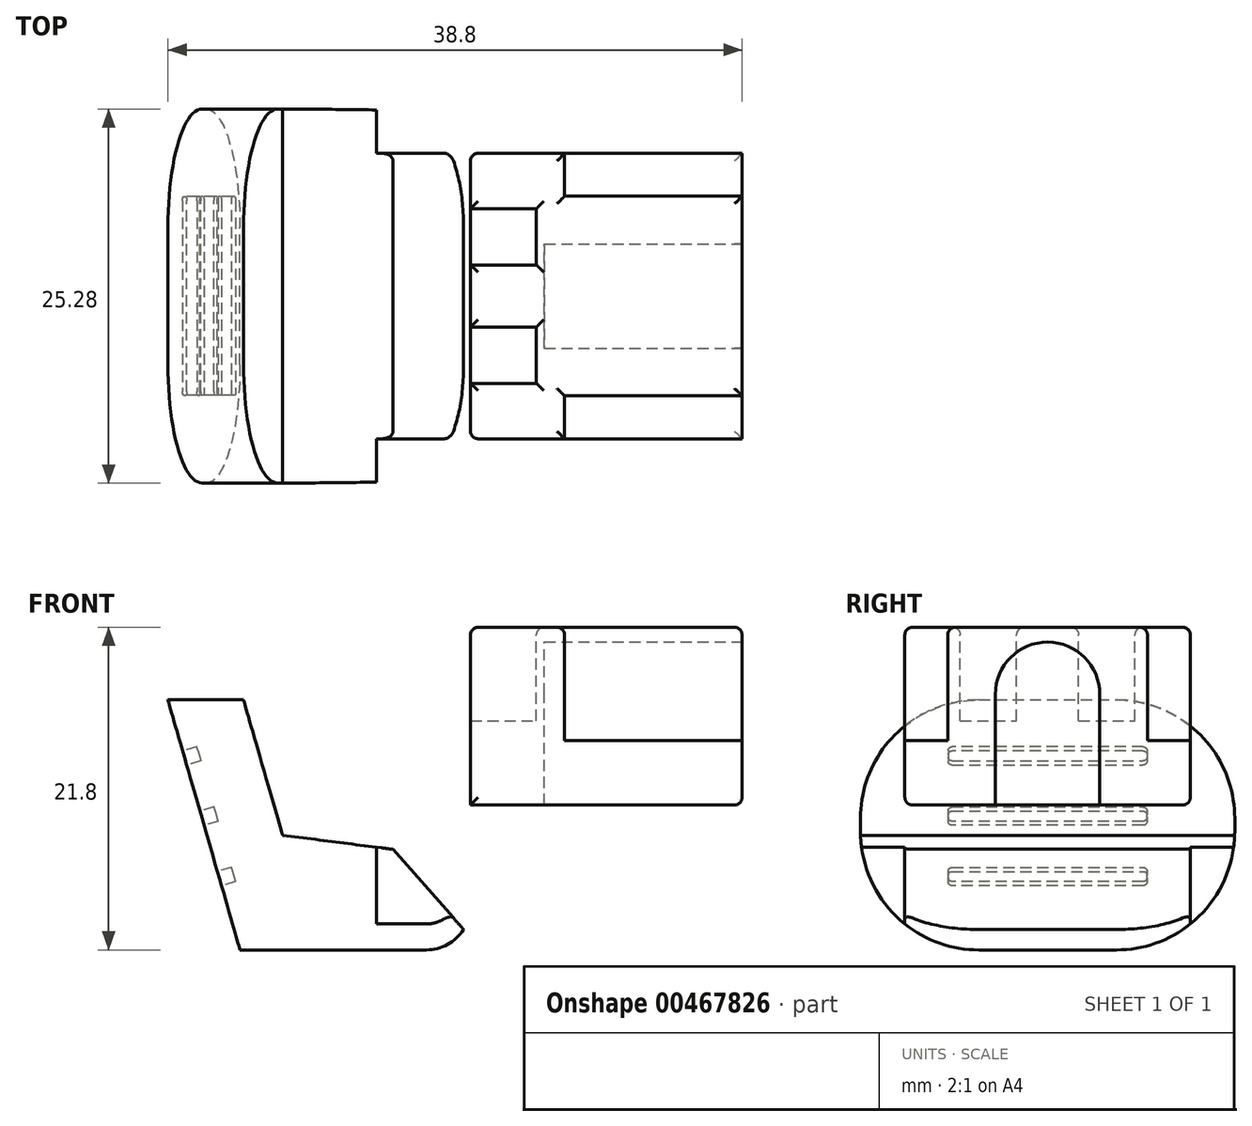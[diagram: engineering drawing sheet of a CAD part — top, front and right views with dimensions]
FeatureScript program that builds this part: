
annotation { "Feature Type Name" : "Feature", "Feature Type Description" : "" }
export const myFeature = defineFeature(function(context is Context, id is Id, definition is map)
    precondition{}
    {
        {
            var Q0;
            Q0=qCreatedBy(makeId("Front.planeOp"),FACE);
            var sketch = newSketch(context, id + "F0", { "sketchPlane" : qUnion([Q0])});
            skLineSegment(sketch, "E0.bottom", {"start": v(-5.4, 12) * mm, "end": v(12.95, 12) * mm});
            skLineSegment(sketch, "E0.top", {"start": v(-5.4, 0) * mm, "end": v(12.95, 0) * mm});
            skLineSegment(sketch, "E0.left", {"start": v(-5.4, 12) * mm, "end": v(-5.4, 0) * mm});
            skLineSegment(sketch, "E0.right", {"start": v(12.95, 12) * mm, "end": v(12.95, 0) * mm});
            skLineSegment(sketch, "E1.bottom", {"start": v(-5.4, 0) * mm, "end": v(-1.18, 0) * mm});
            skLineSegment(sketch, "E1.top", {"start": v(-5.4, -9.8) * mm, "end": v(-1.18, -9.8) * mm});
            skLineSegment(sketch, "E1.left", {"start": v(-5.4, 0) * mm, "end": v(-5.4, -9.8) * mm});
            skLineSegment(sketch, "E1.right", {"start": v(-1.18, 0) * mm, "end": v(-1.18, -9.8) * mm});
            skLineSegment(sketch, "E2", {"start": v(-5.4, -3.67) * mm, "end": v(-18.1, -2.05) * mm});
            skLineSegment(sketch, "E3", {"start": v(-5.4, -9.8) * mm, "end": v(-20.98, -9.8) * mm});
            skLineSegment(sketch, "E4", {"start": v(-20.98, -9.8) * mm, "end": v(-25.85, 7.1) * mm});
            skLineSegment(sketch, "E5", {"start": v(-25.85, 7.1) * mm, "end": v(-20.74, 7.1) * mm});
            skLineSegment(sketch, "E6", {"start": v(-20.74, 7.1) * mm, "end": v(-18.1, -2.05) * mm});
            skSolve(sketch);
        }
        {
            var Q0;
            Q0=makeQuery(id+"F0.imprint","IMPRINT",FACE,{"disambiguationData":[TD([[makeQuery(id+"F0.imprint","IMPRINT",EDGE,{"derivedFrom":sQuery(id+"F0.wireOp",EDGE,"E0.bottom")}),-1.0]])]});
            var Q1;
            {var subQ3=sQuery(id+"F0.wireOp",EDGE,"E1.bottom");Q1=makeQuery(id+"F0.imprint","IMPRINT",FACE,{"disambiguationData":[TD([[makeQuery(id+"F0.imprint","IMPRINT",EDGE,{"derivedFrom":subQ3}),-1.0]])]});}
            var Q2;
            {var subQ1=sQuery(id+"F0.wireOp",EDGE,"E2");Q2=makeQuery(id+"F0.imprint","IMPRINT",FACE,{"disambiguationData":[TD([[makeQuery(id+"F0.imprint","IMPRINT",EDGE,{"derivedFrom":subQ1}),1.0]])]});}
            extrude(context, id + "F1", {"entities" : qUnion([Q0, Q1, Q2]), "endBound" : BoundingType.SYMMETRIC, "depth" : 25.29 * mm});
        }
        {
            var Q0;
            Q0=makeQuery(id+"F1.opExtrude","SWEPT_FACE",FACE,{"disambiguationData":[OSD([sQuery(id+"F0.wireOp",EDGE,"E0.bottom")])]});
            var sketch = newSketch(context, id + "F2", { "sketchPlane" : qUnion([Q0])});
            skLineSegment(sketch, "E7.bottom", {"start": v(12.95, 12.64) * mm, "end": v(-11.75, 12.64) * mm});
            skLineSegment(sketch, "E7.top", {"start": v(12.95, 9.65) * mm, "end": v(-11.75, 9.65) * mm});
            skLineSegment(sketch, "E7.left", {"start": v(12.95, 12.64) * mm, "end": v(12.95, 9.64) * mm});
            skLineSegment(sketch, "E7.right", {"start": v(-11.75, 12.64) * mm, "end": v(-11.75, 9.64) * mm});
            skLineSegment(sketch, "E8.bottom", {"start": v(12.95, -12.64) * mm, "end": v(-11.75, -12.65) * mm});
            skLineSegment(sketch, "E8.top", {"start": v(12.95, -9.65) * mm, "end": v(-11.75, -9.65) * mm});
            skLineSegment(sketch, "E8.left", {"start": v(12.95, -12.64) * mm, "end": v(12.95, -9.65) * mm});
            skLineSegment(sketch, "E8.right", {"start": v(-11.75, -12.65) * mm, "end": v(-11.75, -9.65) * mm});
            skSolve(sketch);
        }
        {
            var Q0;
            Q0 = qSketchRegion(id + "F2", true);
            extrude(context, id + "F3", {"entities" : qUnion([Q0]), "operationType" : NewBodyOperationType.REMOVE, "oppositeDirection" : true, "depth" : 25 * mm});
        }
        {
            var Q0;
            Q0=makeQuery(id+"F1.opExtrude","SWEPT_FACE",FACE,{"disambiguationData":[OSD([sQuery(id+"F0.wireOp",EDGE,"E0.bottom")])]});
            var sketch = newSketch(context, id + "F4", { "sketchPlane" : qUnion([Q0])});
            skLineSegment(sketch, "E9.bottom", {"start": v(-5.4, 5.9) * mm, "end": v(-0.95, 5.9) * mm});
            skLineSegment(sketch, "E9.top", {"start": v(-5.4, 2.1) * mm, "end": v(-0.95, 2.1) * mm});
            skLineSegment(sketch, "E9.left", {"start": v(-5.4, 5.9) * mm, "end": v(-5.4, 2.1) * mm});
            skLineSegment(sketch, "E9.right", {"start": v(-0.95, 5.9) * mm, "end": v(-0.95, 2.1) * mm});
            skLineSegment(sketch, "E10.MirrorCS", {"start": v(-0.95, -5.9) * mm, "end": v(-0.95, -2.1) * mm});
            skLineSegment(sketch, "E11.MirrorCS", {"start": v(-5.4, -5.9) * mm, "end": v(-5.4, -2.1) * mm});
            skLineSegment(sketch, "E12.MirrorCS", {"start": v(-5.4, -5.9) * mm, "end": v(-0.95, -5.9) * mm});
            skLineSegment(sketch, "E13.MirrorCS", {"start": v(-5.4, -2.1) * mm, "end": v(-0.95, -2.1) * mm});
            skLineSegment(sketch, "E14.bottom", {"start": v(12.95, 9.65) * mm, "end": v(0.95, 9.65) * mm});
            skLineSegment(sketch, "E14.top", {"start": v(12.95, 6.75) * mm, "end": v(0.95, 6.74) * mm});
            skLineSegment(sketch, "E14.left", {"start": v(12.95, 9.65) * mm, "end": v(12.95, 6.75) * mm});
            skLineSegment(sketch, "E14.right", {"start": v(0.95, 9.65) * mm, "end": v(0.95, 6.75) * mm});
            skLineSegment(sketch, "E15.MirrorCS", {"start": v(12.95, -6.75) * mm, "end": v(0.95, -6.74) * mm});
            skLineSegment(sketch, "E16.MirrorCS", {"start": v(12.95, -9.65) * mm, "end": v(0.95, -9.65) * mm});
            skLineSegment(sketch, "E17.MirrorCS", {"start": v(12.95, -9.65) * mm, "end": v(12.95, -6.75) * mm});
            skLineSegment(sketch, "E18.MirrorCS", {"start": v(0.95, -9.65) * mm, "end": v(0.95, -6.75) * mm});
            skSolve(sketch);
        }
        {
            var Q0;
            Q0=makeQuery(id+"F4.imprint","IMPRINT",FACE,{"disambiguationData":[TD([[makeQuery(id+"F4.imprint","IMPRINT",EDGE,{"derivedFrom":sQuery(id+"F4.wireOp",EDGE,"E9.bottom")}),-1.0]])]});
            var Q1;
            Q1=makeQuery(id+"F4.imprint","IMPRINT",FACE,{"disambiguationData":[TD([[makeQuery(id+"F4.imprint","IMPRINT",EDGE,{"derivedFrom":sQuery(id+"F4.wireOp",EDGE,"E10.MirrorCS")}),1.0]])]});
            extrude(context, id + "F5", {"entities" : qUnion([Q0, Q1]), "operationType" : NewBodyOperationType.REMOVE, "oppositeDirection" : true, "depth" : 6.3 * mm});
        }
        {
            var Q0;
            Q0=makeQuery(id+"F4.imprint","IMPRINT",FACE,{"disambiguationData":[TD([[makeQuery(id+"F4.imprint","IMPRINT",EDGE,{"derivedFrom":sQuery(id+"F4.wireOp",EDGE,"E14.bottom")}),1.0]])]});
            var Q1;
            Q1=makeQuery(id+"F4.imprint","IMPRINT",FACE,{"disambiguationData":[TD([[makeQuery(id+"F4.imprint","IMPRINT",EDGE,{"derivedFrom":sQuery(id+"F4.wireOp",EDGE,"E15.MirrorCS")}),1.0]])]});
            extrude(context, id + "F6", {"entities" : qUnion([Q0, Q1]), "operationType" : NewBodyOperationType.REMOVE, "oppositeDirection" : true, "depth" : 7.65 * mm});
        }
        {
            var Q0;
            Q0=makeQuery(id+"F1.opExtrude","SWEPT_FACE",FACE,{"disambiguationData":[OSD([sQuery(id+"F0.wireOp",EDGE,"E0.right")])]});
            var sketch = newSketch(context, id + "F7", { "sketchPlane" : qUnion([Q0])});
            skLineSegment(sketch, "E19", {"start": v(-3.53, 0) * mm, "end": v(-3.53, 7.47) * mm});
            skPoint(sketch, "E20.startSnap0", {"position": v(-6.75, 8.18) * mm});
            skArc(sketch, "E21", {"start": v(-3.53, 7.47) * mm, "mid": v(-2.5, 9.97) * mm, "end": v(0, 11) * mm});
            skArc(sketch, "E22.MirrorCS", {"start": v(3.53, 7.47) * mm, "mid": v(2.5, 9.97) * mm, "end": v(0, 11) * mm});
            skLineSegment(sketch, "E23.MirrorCS", {"start": v(3.53, 0) * mm, "end": v(3.53, 7.47) * mm});
            skSolve(sketch);
        }
        {
            var Q0;
            {var subQ1=sQuery(id+"F7.wireOp",EDGE,"E19");Q0=makeQuery(id+"F7.imprint","IMPRINT",FACE,{"disambiguationData":[TD([[makeQuery(id+"F7.imprint","IMPRINT",EDGE,{"derivedFrom":subQ1}),-1.0]])]});}
            extrude(context, id + "F8", {"entities" : qUnion([Q0]), "operationType" : NewBodyOperationType.REMOVE, "oppositeDirection" : true, "depth" : 13.36 * mm});
        }
        {
            var Q0;
            Q0=makeQuery(id+"F1.opExtrude","CAP_EDGE",EDGE,{"disambiguationData":[OSD([sQuery(id+"F0.wireOp",EDGE,"E5")])],"isStart":false});
            var Q1;
            Q1=makeQuery(id+"F1.opExtrude","CAP_EDGE",EDGE,{"disambiguationData":[OSD([sQuery(id+"F0.wireOp",EDGE,"E1.top"),sQuery(id+"F0.wireOp",EDGE,"E3")])],"isStart":false});
            var Q2;
            Q2=makeQuery(id+"F1.opExtrude","CAP_EDGE",EDGE,{"disambiguationData":[OSD([sQuery(id+"F0.wireOp",EDGE,"E5")])],"isStart":true});
            var Q3;
            Q3=makeQuery(id+"F1.opExtrude","CAP_EDGE",EDGE,{"disambiguationData":[OSD([sQuery(id+"F0.wireOp",EDGE,"E1.top"),sQuery(id+"F0.wireOp",EDGE,"E3")])],"isStart":true});
            fillet(context, id + "F9", {"entities" : qUnion([Q0, Q1, Q2, Q3]), "radius" : 8 * mm, "tangentPropagation" : true, "allowEdgeOverflow" : false});
        }
        {
            var Q0;
            Q0=makeQuery(id+"F1.opExtrude","SWEPT_FACE",FACE,{"disambiguationData":[OSD([sQuery(id+"F0.wireOp",EDGE,"E4")])]});
            var sketch = newSketch(context, id + "F10", { "sketchPlane" : qUnion([Q0])});
            skLineSegment(sketch, "E24.left", {"start": v(-6.72, 10.12) * mm, "end": v(-6.72, 9.67) * mm});
            skPoint(sketch, "E25.visualSharp", {"position": v(-6.72, 10.4) * mm});
            skArc(sketch, "E25.filletArc", {"start": v(-6.44, 10.4) * mm, "mid": v(-6.64, 10.32) * mm, "end": v(-6.72, 10.12) * mm});
            skPoint(sketch, "E26.visualSharp", {"position": v(-6.72, 9.4) * mm});
            skArc(sketch, "E26.filletArc", {"start": v(-6.72, 9.67) * mm, "mid": v(-6.64, 9.48) * mm, "end": v(-6.44, 9.4) * mm});
            skLineSegment(sketch, "E27", {"start": v(0, 9.4) * mm, "end": v(0, 10.4) * mm});
            skLineSegment(sketch, "E28", {"start": v(-6.44, 10.4) * mm, "end": v(0, 10.4) * mm});
            skLineSegment(sketch, "E29", {"start": v(0, 9.4) * mm, "end": v(-6.44, 9.4) * mm});
            skLineSegment(sketch, "E30.MirrorCS", {"start": v(6.72, 10.12) * mm, "end": v(6.72, 9.67) * mm});
            skArc(sketch, "E31.MirrorCS", {"start": v(6.44, 10.4) * mm, "mid": v(6.64, 10.32) * mm, "end": v(6.72, 10.12) * mm});
            skArc(sketch, "E32.MirrorCS", {"start": v(6.72, 9.67) * mm, "mid": v(6.64, 9.48) * mm, "end": v(6.44, 9.4) * mm});
            skPoint(sketch, "E33.MirrorP", {"position": v(6.72, 9.4) * mm});
            skLineSegment(sketch, "E34.MirrorCS", {"start": v(0, 9.4) * mm, "end": v(6.44, 9.4) * mm});
            skLineSegment(sketch, "E35.MirrorCS", {"start": v(6.44, 10.4) * mm, "end": v(0, 10.4) * mm});
            skPoint(sketch, "E36.MirrorP", {"position": v(6.72, 10.4) * mm});
            skLineSegment(sketch, "E37.MirrorCS", {"start": v(-6.72, 1.19) * mm, "end": v(-6.72, 1.64) * mm});
            skArc(sketch, "E38.MirrorCS", {"start": v(-6.44, 0.91) * mm, "mid": v(-6.64, 1) * mm, "end": v(-6.72, 1.19) * mm});
            skArc(sketch, "E39.MirrorCS", {"start": v(-6.72, 1.64) * mm, "mid": v(-6.64, 1.83) * mm, "end": v(-6.44, 1.91) * mm});
            skArc(sketch, "E40.MirrorCS", {"start": v(6.72, 1.64) * mm, "mid": v(6.64, 1.83) * mm, "end": v(6.44, 1.91) * mm});
            skArc(sketch, "E41.MirrorCS", {"start": v(6.44, 0.91) * mm, "mid": v(6.64, 1) * mm, "end": v(6.72, 1.19) * mm});
            skLineSegment(sketch, "E42.MirrorCS", {"start": v(6.72, 1.19) * mm, "end": v(6.72, 1.64) * mm});
            skLineSegment(sketch, "E43.MirrorCS", {"start": v(0, 1.91) * mm, "end": v(0, 0.91) * mm});
            skPoint(sketch, "E44.MirrorP", {"position": v(-6.72, 0.91) * mm});
            skLineSegment(sketch, "E45.MirrorCS", {"start": v(0, 1.91) * mm, "end": v(6.44, 1.91) * mm});
            skLineSegment(sketch, "E46.MirrorCS", {"start": v(-6.44, 0.91) * mm, "end": v(0, 0.91) * mm});
            skPoint(sketch, "E47.MirrorP", {"position": v(6.72, 1.91) * mm});
            skPoint(sketch, "E48.MirrorP", {"position": v(-6.72, 1.91) * mm});
            skLineSegment(sketch, "E49.MirrorCS", {"start": v(0, 1.91) * mm, "end": v(-6.44, 1.91) * mm});
            skLineSegment(sketch, "E50.MirrorCS", {"start": v(6.44, 0.91) * mm, "end": v(0, 0.91) * mm});
            skPoint(sketch, "E51.MirrorP", {"position": v(6.72, 0.91) * mm});
            skLineSegment(sketch, "E52.MirrorCS", {"start": v(-6.72, 5.43) * mm, "end": v(-6.72, 5.88) * mm});
            skLineSegment(sketch, "E53.MirrorCS", {"start": v(6.72, 5.43) * mm, "end": v(6.72, 5.88) * mm});
            skArc(sketch, "E54.MirrorCS", {"start": v(6.44, 5.16) * mm, "mid": v(6.64, 5.24) * mm, "end": v(6.72, 5.43) * mm});
            skArc(sketch, "E55.MirrorCS", {"start": v(-6.44, 5.16) * mm, "mid": v(-6.64, 5.24) * mm, "end": v(-6.72, 5.43) * mm});
            skArc(sketch, "E56.MirrorCS", {"start": v(-6.72, 5.88) * mm, "mid": v(-6.64, 6.08) * mm, "end": v(-6.44, 6.16) * mm});
            skLineSegment(sketch, "E57.MirrorCS", {"start": v(0, 6.16) * mm, "end": v(0, 5.16) * mm});
            skArc(sketch, "E58.MirrorCS", {"start": v(6.72, 5.88) * mm, "mid": v(6.64, 6.08) * mm, "end": v(6.44, 6.16) * mm});
            skLineSegment(sketch, "E59.MirrorCS", {"start": v(-6.44, 5.16) * mm, "end": v(0, 5.16) * mm});
            skLineSegment(sketch, "E60.MirrorCS", {"start": v(0, 6.16) * mm, "end": v(-6.44, 6.16) * mm});
            skPoint(sketch, "E61.MirrorP", {"position": v(-6.72, 6.16) * mm});
            skLineSegment(sketch, "E62.MirrorCS", {"start": v(0, 6.16) * mm, "end": v(6.44, 6.16) * mm});
            skLineSegment(sketch, "E63.MirrorCS", {"start": v(6.44, 5.16) * mm, "end": v(0, 5.16) * mm});
            skPoint(sketch, "E64.MirrorP", {"position": v(6.72, 5.16) * mm});
            skPoint(sketch, "E65.MirrorP", {"position": v(6.72, 6.16) * mm});
            skPoint(sketch, "E66.MirrorP", {"position": v(-6.72, 5.16) * mm});
            skSolve(sketch);
        }
        {
            var Q0;
            Q0 = qSketchRegion(id + "F10", true);
            extrude(context, id + "F11", {"entities" : qUnion([Q0]), "operationType" : NewBodyOperationType.REMOVE, "oppositeDirection" : true, "depth" : 1 * mm});
        }
        {
            var Q0;
            Q0=makeQuery(id+"F1.opExtrude","SWEPT_EDGE",EDGE,{"disambiguationData":[OSD([sQuery(id+"F0.wireOp",EDGE,"E1.left"),sQuery(id+"F0.wireOp",EDGE,"E2")])]});
            chamfer(context, id + "F12", {"entities" : qUnion([Q0]), "width" : 6 * mm, "tangentPropagation" : true});
        }
        {
            var Q0;
            Q0=makeQuery(id+"F1.opExtrude","SWEPT_EDGE",EDGE,{"disambiguationData":[OSD([sQuery(id+"F0.wireOp",EDGE,"E1.top"),sQuery(id+"F0.wireOp",EDGE,"E1.right")])]});
            fillet(context, id + "F13", {"entities" : qUnion([Q0]), "radius" : 3 * mm, "tangentPropagation" : true, "allowEdgeOverflow" : false});
        }
        {
            var Q0;
            Q0=makeQuery(id+"F1.opExtrude","SWEPT_FACE",FACE,{"disambiguationData":[OSD([sQuery(id+"F0.wireOp",EDGE,"E0.bottom")])]});
            var Q1;
            Q1=makeQuery(id+"F6.boolean.opBoolean","COPY",EDGE,{"derivedFrom":makeQuery(id+"F6.opExtrude","CAP_EDGE",EDGE,{"disambiguationData":[OSD([sQuery(id+"F4.wireOp",EDGE,"E16.MirrorCS")])],"isStart":false})});
            var Q2;
            Q2=makeQuery(id+"F3.boolean.opBoolean","INTERSECT",EDGE,{"derivedFrom":[makeQuery(id+"F1.opExtrude","SWEPT_FACE",FACE,{"disambiguationData":[OSD([sQuery(id+"F0.wireOp",EDGE,"E0.top")])]}),makeQuery(id+"F3.opExtrude","SWEPT_FACE",FACE,{"disambiguationData":[OSD([sQuery(id+"F2.wireOp",EDGE,"E8.top")])]})]});
            var Q3;
            Q3=makeQuery(id+"F6.boolean.opBoolean","COPY",EDGE,{"derivedFrom":makeQuery(id+"F6.opExtrude","SWEPT_EDGE",EDGE,{"disambiguationData":[OSD([sQuery(id+"F0.wireOp",EDGE,"E0.bottom"),sQuery(id+"F0.wireOp",EDGE,"E0.right"),sQuery(id+"F4.wireOp",EDGE,"E15.MirrorCS"),sQuery(id+"F4.wireOp",EDGE,"E17.MirrorCS")])]})});
            var Q4;
            Q4=makeQuery(id+"F3.boolean.opBoolean","INTERSECT",EDGE,{"derivedFrom":[makeQuery(id+"F1.opExtrude","SWEPT_FACE",FACE,{"disambiguationData":[OSD([sQuery(id+"F0.wireOp",EDGE,"E0.top")])]}),makeQuery(id+"F3.opExtrude","SWEPT_FACE",FACE,{"disambiguationData":[OSD([sQuery(id+"F2.wireOp",EDGE,"E7.top")])]})]});
            var Q5;
            Q5=makeQuery(id+"F3.boolean.opBoolean","COPY",EDGE,{"derivedFrom":makeQuery(id+"F3.opExtrude","SWEPT_EDGE",EDGE,{"disambiguationData":[OSD([sQuery(id+"F0.wireOp",EDGE,"E0.bottom"),sQuery(id+"F0.wireOp",EDGE,"E0.right"),sQuery(id+"F2.wireOp",EDGE,"E7.top"),sQuery(id+"F2.wireOp",EDGE,"E7.left")])]})});
            var Q6;
            Q6=makeQuery(id+"F6.boolean.opBoolean","COPY",EDGE,{"derivedFrom":makeQuery(id+"F6.opExtrude","CAP_EDGE",EDGE,{"disambiguationData":[OSD([sQuery(id+"F4.wireOp",EDGE,"E14.bottom")])],"isStart":false})});
            var Q7;
            Q7=makeQuery(id+"F6.boolean.opBoolean","COPY",EDGE,{"derivedFrom":makeQuery(id+"F6.opExtrude","CAP_EDGE",EDGE,{"disambiguationData":[OSD([sQuery(id+"F4.wireOp",EDGE,"E14.left")])],"isStart":false})});
            var Q8;
            {var subQ0=sQuery(id+"F0.wireOp",EDGE,"E0.top");var subQ1=sQuery(id+"F0.wireOp",EDGE,"E0.right");Q8=makeQuery(id+"F8.boolean.opBoolean","SPLIT",EDGE,{"disambiguationData":[TD([makeQuery(id+"F3.boolean.opBoolean","COPY",FACE,{"derivedFrom":makeQuery(id+"F3.opExtrude","SWEPT_FACE",FACE,{"disambiguationData":[OSD([sQuery(id+"F2.wireOp",EDGE,"E7.top")])]})})])],"derivedFrom":makeQuery(id+"F1.opExtrude","SWEPT_EDGE",EDGE,{"disambiguationData":[OSD([subQ0,subQ1])]})});}
            var Q9;
            {var subQ0=sQuery(id+"F0.wireOp",EDGE,"E0.top");var subQ1=sQuery(id+"F0.wireOp",EDGE,"E0.right");Q9=makeQuery(id+"F8.boolean.opBoolean","SPLIT",EDGE,{"disambiguationData":[TD([makeQuery(id+"F3.boolean.opBoolean","COPY",FACE,{"derivedFrom":makeQuery(id+"F3.opExtrude","SWEPT_FACE",FACE,{"disambiguationData":[OSD([sQuery(id+"F2.wireOp",EDGE,"E8.top")])]})})])],"derivedFrom":makeQuery(id+"F1.opExtrude","SWEPT_EDGE",EDGE,{"disambiguationData":[OSD([subQ0,subQ1])]})});}
            var Q10;
            Q10=makeQuery(id+"F8.boolean.opBoolean","COPY",EDGE,{"derivedFrom":makeQuery(id+"F8.opExtrude","SWEPT_EDGE",EDGE,{"disambiguationData":[OSD([sQuery(id+"F0.wireOp",EDGE,"E0.top"),sQuery(id+"F0.wireOp",EDGE,"E0.right"),sQuery(id+"F7.wireOp",EDGE,"E19")])]})});
            var Q11;
            Q11=makeQuery(id+"F8.boolean.opBoolean","COPY",EDGE,{"derivedFrom":makeQuery(id+"F8.opExtrude","SWEPT_EDGE",EDGE,{"disambiguationData":[OSD([sQuery(id+"F0.wireOp",EDGE,"E0.top"),sQuery(id+"F0.wireOp",EDGE,"E0.right"),sQuery(id+"F7.wireOp",EDGE,"E23.MirrorCS")])]})});
            var Q12;
            Q12=makeQuery(id+"F6.boolean.opBoolean","COPY",EDGE,{"derivedFrom":makeQuery(id+"F6.opExtrude","SWEPT_EDGE",EDGE,{"disambiguationData":[OSD([sQuery(id+"F0.wireOp",EDGE,"E0.bottom"),sQuery(id+"F0.wireOp",EDGE,"E0.right"),sQuery(id+"F4.wireOp",EDGE,"E14.top"),sQuery(id+"F4.wireOp",EDGE,"E14.left")])]})});
            var Q13;
            Q13=makeQuery(id+"F6.boolean.opBoolean","COPY",EDGE,{"derivedFrom":makeQuery(id+"F6.opExtrude","SWEPT_EDGE",EDGE,{"disambiguationData":[OSD([sQuery(id+"F2.wireOp",EDGE,"E7.top"),sQuery(id+"F4.wireOp",EDGE,"E14.bottom"),sQuery(id+"F4.wireOp",EDGE,"E14.right")])]})});
            var Q14;
            Q14=makeQuery(id+"F12.opChamfer","BLEND_EDGE",EDGE,{"blendedFrom":[makeQuery(id+"F1.opExtrude","SWEPT_EDGE",EDGE,{"disambiguationData":[OSD([sQuery(id+"F0.wireOp",EDGE,"E1.left"),sQuery(id+"F0.wireOp",EDGE,"E2")])]}),makeQuery(id+"F3.boolean.opBoolean","COPY",FACE,{"derivedFrom":makeQuery(id+"F3.opExtrude","SWEPT_FACE",FACE,{"disambiguationData":[OSD([sQuery(id+"F2.wireOp",EDGE,"E7.top")])]})})],"blendedInto":[makeQuery(id+"F3.boolean.opBoolean","COPY",FACE,{"derivedFrom":makeQuery(id+"F3.opExtrude","SWEPT_FACE",FACE,{"disambiguationData":[OSD([sQuery(id+"F2.wireOp",EDGE,"E7.top")])]})})]});
            var Q15;
            Q15=makeQuery(id+"F3.boolean.opBoolean","INTERSECT",EDGE,{"derivedFrom":[makeQuery(id+"F1.opExtrude","SWEPT_FACE",FACE,{"disambiguationData":[OSD([sQuery(id+"F0.wireOp",EDGE,"E0.left"),sQuery(id+"F0.wireOp",EDGE,"E1.left")])]}),makeQuery(id+"F3.opExtrude","SWEPT_FACE",FACE,{"disambiguationData":[OSD([sQuery(id+"F2.wireOp",EDGE,"E7.top")])]})]});
            var Q16;
            Q16=makeQuery(id+"F12.opChamfer","BLEND_EDGE",EDGE,{"blendedFrom":[makeQuery(id+"F1.opExtrude","SWEPT_EDGE",EDGE,{"disambiguationData":[OSD([sQuery(id+"F0.wireOp",EDGE,"E1.left"),sQuery(id+"F0.wireOp",EDGE,"E2")])]}),makeQuery(id+"F3.boolean.opBoolean","COPY",FACE,{"derivedFrom":makeQuery(id+"F3.opExtrude","SWEPT_FACE",FACE,{"disambiguationData":[OSD([sQuery(id+"F2.wireOp",EDGE,"E8.top")])]})})],"blendedInto":[makeQuery(id+"F3.boolean.opBoolean","COPY",FACE,{"derivedFrom":makeQuery(id+"F3.opExtrude","SWEPT_FACE",FACE,{"disambiguationData":[OSD([sQuery(id+"F2.wireOp",EDGE,"E8.top")])]})})]});
            var Q17;
            Q17=makeQuery(id+"F3.boolean.opBoolean","INTERSECT",EDGE,{"derivedFrom":[makeQuery(id+"F1.opExtrude","SWEPT_FACE",FACE,{"disambiguationData":[OSD([sQuery(id+"F0.wireOp",EDGE,"E0.left"),sQuery(id+"F0.wireOp",EDGE,"E1.left")])]}),makeQuery(id+"F3.opExtrude","SWEPT_FACE",FACE,{"disambiguationData":[OSD([sQuery(id+"F2.wireOp",EDGE,"E8.top")])]})]});
            var Q18;
            Q18=makeQuery(id+"F6.boolean.opBoolean","COPY",EDGE,{"derivedFrom":makeQuery(id+"F6.opExtrude","SWEPT_EDGE",EDGE,{"disambiguationData":[OSD([sQuery(id+"F2.wireOp",EDGE,"E8.top"),sQuery(id+"F4.wireOp",EDGE,"E16.MirrorCS"),sQuery(id+"F4.wireOp",EDGE,"E18.MirrorCS")])]})});
            fillet(context, id + "F14", {"entities" : qUnion([Q0, Q1, Q2, Q3, Q4, Q5, Q6, Q7, Q8, Q9, Q10, Q11, Q12, Q13, Q14, Q15, Q16, Q17, Q18]), "radius" : 0.5 * mm, "tangentPropagation" : true, "allowEdgeOverflow" : false});
        }
    });
